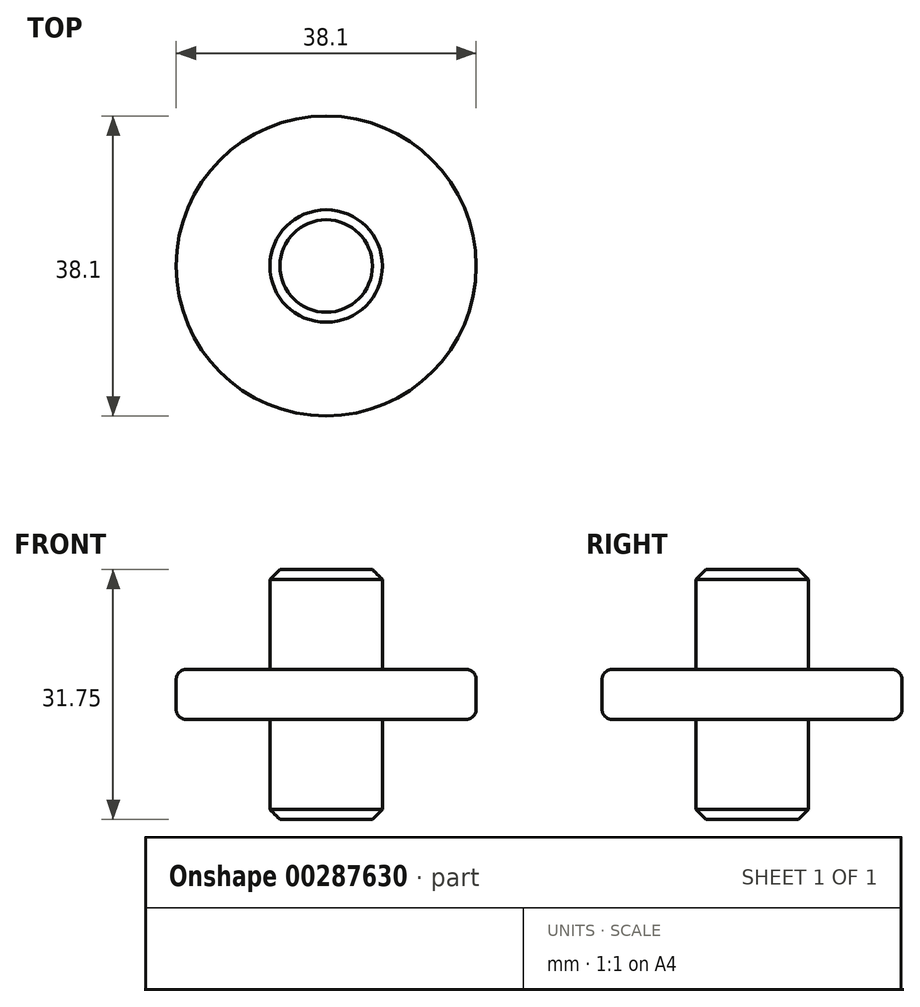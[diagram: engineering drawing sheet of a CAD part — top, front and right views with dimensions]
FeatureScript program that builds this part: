
annotation { "Feature Type Name" : "Feature", "Feature Type Description" : "" }
export const myFeature = defineFeature(function(context is Context, id is Id, definition is map)
    precondition{}
    {
        {
            var Q0;
            Q0=qCreatedBy(makeId("Front.planeOp"),FACE);
            var sketch = newSketch(context, id + "F0", { "sketchPlane" : qUnion([Q0])});
            skLineSegment(sketch, "E0", {"start": v(0, 19.05) * mm, "end": v(7.14, 19.05) * mm});
            skLineSegment(sketch, "E1", {"start": v(7.14, 19.05) * mm, "end": v(7.14, 6.35) * mm});
            skLineSegment(sketch, "E2", {"start": v(7.14, 6.35) * mm, "end": v(19.05, 6.35) * mm});
            skLineSegment(sketch, "E3", {"start": v(19.05, 6.35) * mm, "end": v(19.05, 0) * mm});
            skLineSegment(sketch, "E4", {"start": v(19.05, 0) * mm, "end": v(7.14, 0) * mm});
            skLineSegment(sketch, "E5", {"start": v(7.14, 0) * mm, "end": v(7.14, -12.7) * mm});
            skLineSegment(sketch, "E6", {"start": v(7.14, -12.7) * mm, "end": v(0, -12.7) * mm});
            skLineSegment(sketch, "E7", {"start": v(0, 19.05) * mm, "end": v(0, -12.7) * mm, "construction": true});
            skLineSegment(sketch, "E8", {"start": v(0, 19.05) * mm, "end": v(0, -12.7) * mm});
            skSolve(sketch);
        }
        {
            var Q0;
            Q0 = qSketchRegion(id + "F0", true);
            var Q1;
            Q1=sQuery(id+"F0.wireOp",EDGE,"E8");
            revolve(context, id + "F1", {"entities" : qUnion([Q0]), "axis" : qUnion([Q1]), "revolveType" : RevolveType.FULL});
        }
        {
            var Q0;
            Q0=makeQuery(id+"F1.opRevolve","SWEPT_EDGE",EDGE,{"disambiguationData":[OSD([sQuery(id+"F0.wireOp",EDGE,"E2"),sQuery(id+"F0.wireOp",EDGE,"E3")])]});
            var Q1;
            Q1=makeQuery(id+"F1.opRevolve","SWEPT_EDGE",EDGE,{"disambiguationData":[OSD([sQuery(id+"F0.wireOp",EDGE,"E3"),sQuery(id+"F0.wireOp",EDGE,"E4")])]});
            fillet(context, id + "F2", {"entities" : qUnion([Q0, Q1]), "radius" : 1.27 * mm, "tangentPropagation" : true, "allowEdgeOverflow" : false});
        }
        {
            var Q0;
            Q0=makeQuery(id+"F1.opRevolve","SWEPT_EDGE",EDGE,{"disambiguationData":[OSD([sQuery(id+"F0.wireOp",EDGE,"E0"),sQuery(id+"F0.wireOp",EDGE,"E1")])]});
            var Q1;
            Q1=makeQuery(id+"F1.opRevolve","SWEPT_EDGE",EDGE,{"disambiguationData":[OSD([sQuery(id+"F0.wireOp",EDGE,"E5"),sQuery(id+"F0.wireOp",EDGE,"E6")])]});
            chamfer(context, id + "F3", {"entities" : qUnion([Q0, Q1]), "width" : 1.27 * mm, "tangentPropagation" : true});
        }
    });
